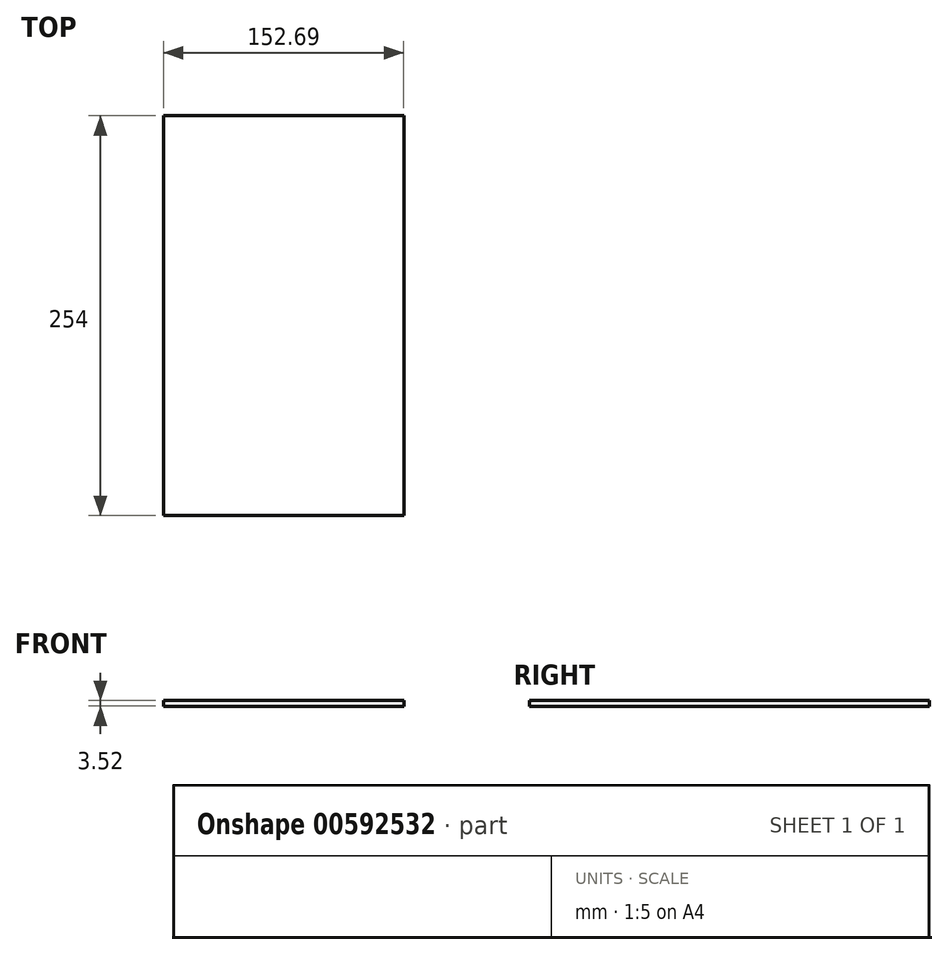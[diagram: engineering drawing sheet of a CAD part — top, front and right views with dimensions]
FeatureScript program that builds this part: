
annotation { "Feature Type Name" : "Feature", "Feature Type Description" : "" }
export const myFeature = defineFeature(function(context is Context, id is Id, definition is map)
    precondition{}
    {
        {
            var Q0;
            Q0=qCreatedBy(makeId("Front.planeOp"),FACE);
            var sketch = newSketch(context, id + "F0", { "sketchPlane" : qUnion([Q0])});
            skLineSegment(sketch, "E0.bottom", {"start": v(-76.14, -76.34) * mm, "end": v(76.55, -76.34) * mm});
            skLineSegment(sketch, "E0.top", {"start": v(-76.14, -72.82) * mm, "end": v(76.55, -72.82) * mm});
            skLineSegment(sketch, "E0.left", {"start": v(-76.14, -76.34) * mm, "end": v(-76.14, -72.82) * mm});
            skLineSegment(sketch, "E0.right", {"start": v(76.55, -76.34) * mm, "end": v(76.55, -72.82) * mm});
            skSolve(sketch);
        }
        {
            var Q0;
            Q0 = qSketchRegion(id + "F0", true);
            extrude(context, id + "F1", {"entities" : qUnion([Q0]), "depth" : 254 * mm, "offsetDistance" : 25.4 * mm});
        }
    });
